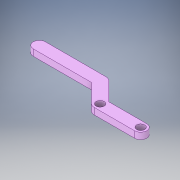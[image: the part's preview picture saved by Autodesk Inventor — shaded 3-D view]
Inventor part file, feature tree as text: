
AUTODESK INVENTOR PART (.ipt)
format: ipt  version: 2019 (Build 230136000, 136)  size: 134,656 bytes
history: native  units: mm
features: other x1, extrude x1, sketch x1
ambient origin geometry x8: Origin, YZ Plane, XZ Plane, XY Plane, X Axis, Y Axis, Z Axis, Center Point
bodies: Body1 (feature_tree)
feature tree (3):
  other  "Sólido1"
  extrude  "Extrusión1"  Depth=6.0mm
  sketch  "Boceto1"  dims[d0=4.0mm d1=6.0mm d2=20.0mm d3=4.0mm d4=6.0mm d5=5.0mm d6=5.0mm d7=6.0mm d8=30.0mm d9=3.18mm d10=0.0mm]
